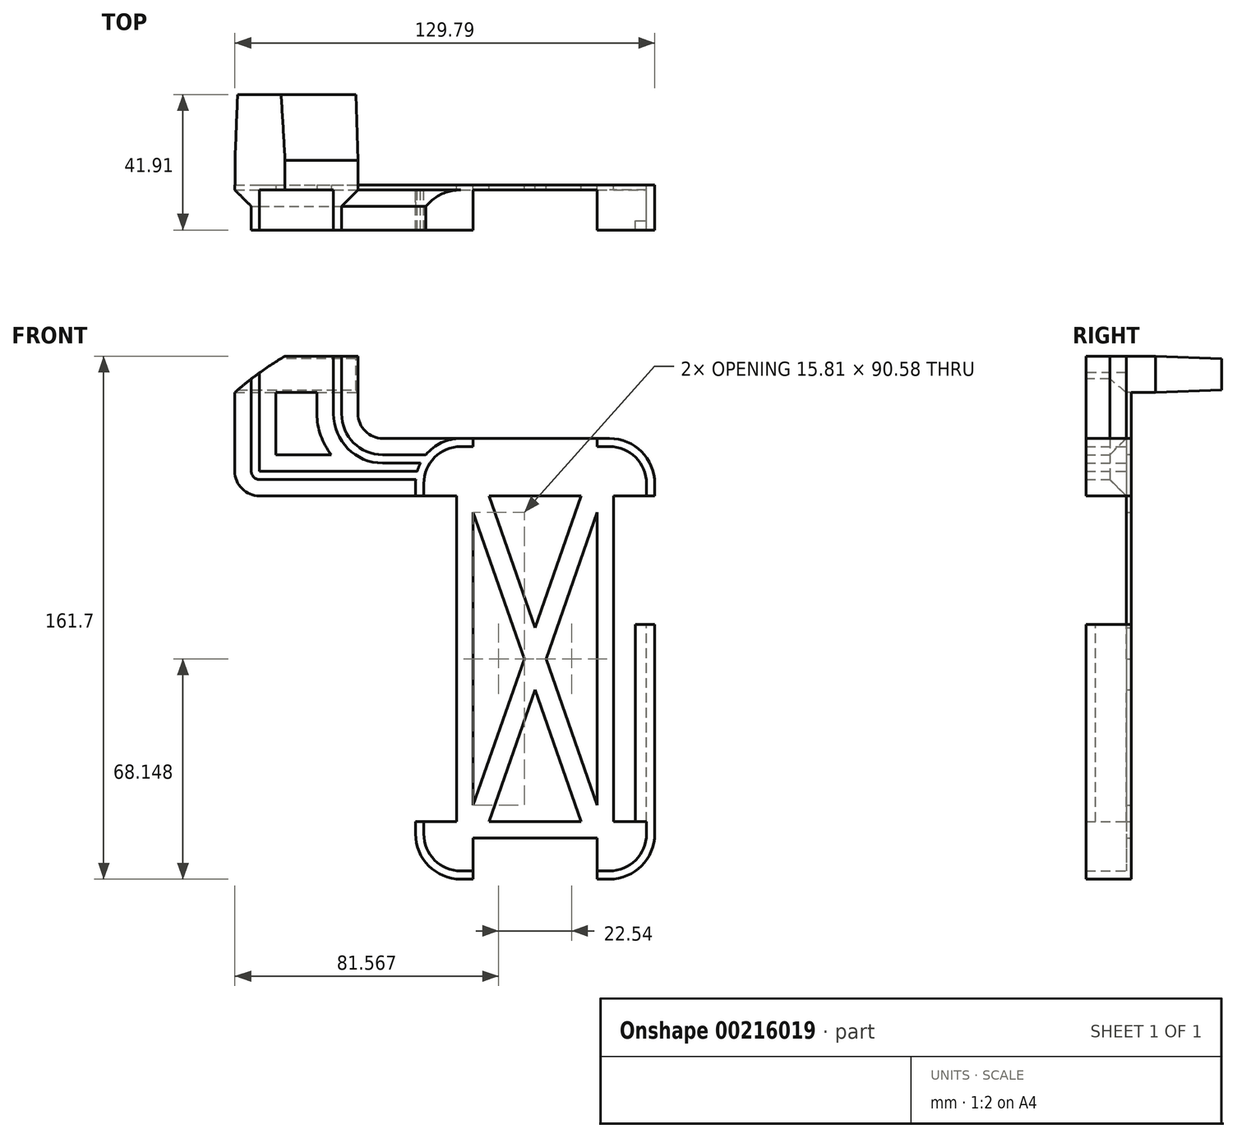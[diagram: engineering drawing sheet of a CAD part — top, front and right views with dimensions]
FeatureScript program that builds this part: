
annotation { "Feature Type Name" : "Feature", "Feature Type Description" : "" }
export const myFeature = defineFeature(function(context is Context, id is Id, definition is map)
    precondition{}
    {
        {
            var Q0;
            Q0=qCreatedBy(makeId("Front.planeOp"),FACE);
            var sketch = newSketch(context, id + "F0", { "sketchPlane" : qUnion([Q0])});
            skLineSegment(sketch, "E0.bottom", {"start": v(-38.1, 11.18) * mm, "end": v(0, 11.18) * mm});
            skLineSegment(sketch, "E0.top", {"start": v(-38.1, 0) * mm, "end": v(0, 0) * mm});
            skLineSegment(sketch, "E0.left", {"start": v(-38.1, 11.18) * mm, "end": v(-38.1, 0) * mm});
            skLineSegment(sketch, "E0.right", {"start": v(0, 11.18) * mm, "end": v(0, 0) * mm});
            skSolve(sketch);
        }
        {
            var Q0;
            Q0=makeQuery(id+"F0.imprint","IMPRINT",FACE,{"disambiguationData":[TD([[makeQuery(id+"F0.imprint","IMPRINT",EDGE,{"derivedFrom":sQuery(id+"F0.wireOp",EDGE,"E0.bottom")}),-1.0]])]});
            extrude(context, id + "F1", {"entities" : qUnion([Q0]), "oppositeDirection" : true, "depth" : 20.32 * mm, "hasDraft" : true, "draftAngle" : 2 * degree, "draftPullDirection" : true, "hasSecondDirection" : true, "secondDirectionOppositeDirection" : false, "secondDirectionDepth" : 7.62 * mm});
        }
        {
            var Q0;
            Q0=makeQuery(id+"F1.opExtrude","CAP_FACE",FACE,{"disambiguationData":[OSD([sQuery(id+"F0.wireOp",EDGE,"E0.bottom"),sQuery(id+"F0.wireOp",EDGE,"E0.top"),sQuery(id+"F0.wireOp",EDGE,"E0.left"),sQuery(id+"F0.wireOp",EDGE,"E0.right")])],"isStart":true});
            var sketch = newSketch(context, id + "F2", { "sketchPlane" : qUnion([Q0])});
            skLineSegment(sketch, "E1.0", {"start": v(31.75, -16.76) * mm, "end": v(77.72, -16.76) * mm});
            skLineSegment(sketch, "E1.1", {"start": v(20.32, -28.2) * mm, "end": v(20.32, -136.55) * mm});
            skLineSegment(sketch, "E1.2", {"start": v(31.75, -147.98) * mm, "end": v(77.72, -147.98) * mm});
            skLineSegment(sketch, "E1.3", {"start": v(89.15, -28.2) * mm, "end": v(89.15, -136.55) * mm});
            skPoint(sketch, "E2.visualSharp", {"position": v(20.32, -16.76) * mm});
            skArc(sketch, "E2.filletArc", {"start": v(31.75, -16.76) * mm, "mid": v(23.67, -20.11) * mm, "end": v(20.32, -28.2) * mm});
            skPoint(sketch, "E3.visualSharp", {"position": v(89.15, -16.76) * mm});
            skArc(sketch, "E3.filletArc", {"start": v(89.15, -28.2) * mm, "mid": v(85.8, -20.11) * mm, "end": v(77.72, -16.76) * mm});
            skPoint(sketch, "E4.visualSharp", {"position": v(89.15, -147.98) * mm});
            skArc(sketch, "E4.filletArc", {"start": v(77.72, -147.98) * mm, "mid": v(85.8, -144.63) * mm, "end": v(89.15, -136.55) * mm});
            skPoint(sketch, "E5.visualSharp", {"position": v(20.32, -147.98) * mm});
            skArc(sketch, "E5.filletArc", {"start": v(20.32, -136.55) * mm, "mid": v(23.67, -144.63) * mm, "end": v(31.75, -147.98) * mm});
            skArc(sketch, "E6.0", {"start": v(31.75, -14.22) * mm, "mid": v(21.87, -18.32) * mm, "end": v(17.78, -28.2) * mm});
            skLineSegment(sketch, "E6.1", {"start": v(17.78, -28.2) * mm, "end": v(17.78, -136.55) * mm});
            skLineSegment(sketch, "E6.2", {"start": v(31.75, -14.22) * mm, "end": v(77.72, -14.22) * mm});
            skArc(sketch, "E6.3", {"start": v(17.78, -136.55) * mm, "mid": v(21.87, -146.43) * mm, "end": v(31.75, -150.52) * mm});
            skArc(sketch, "E6.4", {"start": v(91.7, -28.2) * mm, "mid": v(87.6, -18.32) * mm, "end": v(77.72, -14.22) * mm});
            skLineSegment(sketch, "E6.5", {"start": v(91.7, -28.2) * mm, "end": v(91.7, -136.55) * mm});
            skArc(sketch, "E6.6", {"start": v(77.72, -150.52) * mm, "mid": v(87.6, -146.43) * mm, "end": v(91.7, -136.55) * mm});
            skLineSegment(sketch, "E6.7", {"start": v(31.75, -150.52) * mm, "end": v(77.72, -150.52) * mm});
            skLineSegment(sketch, "E7", {"start": v(17.78, -32) * mm, "end": v(91.7, -32) * mm});
            skLineSegment(sketch, "E8", {"start": v(35.56, -14.22) * mm, "end": v(35.56, -150.52) * mm});
            skLineSegment(sketch, "E9", {"start": v(73.91, -14.22) * mm, "end": v(73.91, -150.52) * mm});
            skLineSegment(sketch, "E10", {"start": v(17.78, -132.74) * mm, "end": v(91.7, -132.74) * mm});
            skLineSegment(sketch, "E11", {"start": v(30.48, -32) * mm, "end": v(30.48, -132.74) * mm});
            skLineSegment(sketch, "E12", {"start": v(79, -32) * mm, "end": v(79, -132.74) * mm});
            skLineSegment(sketch, "E13", {"start": v(35.56, -26.92) * mm, "end": v(73.91, -26.92) * mm});
            skLineSegment(sketch, "E14", {"start": v(35.56, -137.82) * mm, "end": v(73.91, -137.82) * mm});
            skLineSegment(sketch, "E15", {"start": v(35.56, -37.08) * mm, "end": v(68.96, -132.74) * mm});
            skLineSegment(sketch, "E16", {"start": v(40.51, -32) * mm, "end": v(73.91, -127.66) * mm});
            skLineSegment(sketch, "E17", {"start": v(35.56, -127.66) * mm, "end": v(68.96, -32) * mm});
            skLineSegment(sketch, "E18", {"start": v(40.51, -132.74) * mm, "end": v(73.91, -37.08) * mm});
            skSolve(sketch);
        }
        {
            var Q0;
            {var subQ0=sQuery(id+"F2.wireOp",EDGE,"E2.filletArc");Q0=makeQuery(id+"F2.imprint","IMPRINT",FACE,{"disambiguationData":[TD([[makeQuery(id+"F2.imprint","IMPRINT",EDGE,{"derivedFrom":subQ0}),-1.0]])]});}
            var Q1;
            {var subQ0=sQuery(id+"F2.wireOp",EDGE,"E3.filletArc");Q1=makeQuery(id+"F2.imprint","IMPRINT",FACE,{"disambiguationData":[TD([[makeQuery(id+"F2.imprint","IMPRINT",EDGE,{"derivedFrom":subQ0}),-1.0]])]});}
            var Q2;
            {var subQ4=sQuery(id+"F2.wireOp",EDGE,"E5.filletArc");Q2=makeQuery(id+"F2.imprint","IMPRINT",FACE,{"disambiguationData":[TD([[makeQuery(id+"F2.imprint","IMPRINT",EDGE,{"derivedFrom":subQ4}),-1.0]])]});}
            var Q3;
            {var subQ4=sQuery(id+"F2.wireOp",EDGE,"E4.filletArc");Q3=makeQuery(id+"F2.imprint","IMPRINT",FACE,{"disambiguationData":[TD([[makeQuery(id+"F2.imprint","IMPRINT",EDGE,{"derivedFrom":subQ4}),-1.0]])]});}
            extrude(context, id + "F3", {"entities" : qUnion([Q0, Q1, Q2, Q3]), "depth" : 13.97 * mm});
        }
        {
            var Q0;
            {var subQ4=sQuery(id+"F2.wireOp",EDGE,"E2.filletArc");Q0=makeQuery(id+"F2.imprint","IMPRINT",FACE,{"disambiguationData":[TD([[makeQuery(id+"F2.imprint","IMPRINT",EDGE,{"derivedFrom":subQ4}),1.0]])]});}
            var Q1;
            {var subQ0=sQuery(id+"F2.wireOp",EDGE,"E3.filletArc");Q1=makeQuery(id+"F2.imprint","IMPRINT",FACE,{"disambiguationData":[TD([[makeQuery(id+"F2.imprint","IMPRINT",EDGE,{"derivedFrom":subQ0}),1.0]])]});}
            var Q2;
            {var subQ0=sQuery(id+"F2.wireOp",EDGE,"E5.filletArc");Q2=makeQuery(id+"F2.imprint","IMPRINT",FACE,{"disambiguationData":[TD([[makeQuery(id+"F2.imprint","IMPRINT",EDGE,{"derivedFrom":subQ0}),1.0]])]});}
            var Q3;
            {var subQ0=sQuery(id+"F2.wireOp",EDGE,"E4.filletArc");Q3=makeQuery(id+"F2.imprint","IMPRINT",FACE,{"disambiguationData":[TD([[makeQuery(id+"F2.imprint","IMPRINT",EDGE,{"derivedFrom":subQ0}),1.0]])]});}
            var Q4;
            {var subQ3=sQuery(id+"F2.wireOp",EDGE,"E11");Q4=makeQuery(id+"F2.imprint","IMPRINT",FACE,{"disambiguationData":[TD([[makeQuery(id+"F2.imprint","IMPRINT",EDGE,{"derivedFrom":subQ3}),1.0]])]});}
            var Q5;
            {var subQ5=sQuery(id+"F2.wireOp",EDGE,"E7");var subQ7=sQuery(id+"F2.wireOp",EDGE,"E16");var subQ8=makeQuery(id+"F2.imprint","INTERSECT",VERTEX,{"derivedFrom":[subQ5,subQ7]});Q5=makeQuery(id+"F2.imprint","IMPRINT",FACE,{"disambiguationData":[TD([[makeQuery(id+"F2.imprint","IMPRINT",EDGE,{"disambiguationData":[TD([[subQ8,1.0]])],"derivedFrom":subQ5}),-1.0]])]});}
            var Q6;
            {var subQ3=sQuery(id+"F2.wireOp",EDGE,"E13");Q6=makeQuery(id+"F2.imprint","IMPRINT",FACE,{"disambiguationData":[TD([[makeQuery(id+"F2.imprint","IMPRINT",EDGE,{"derivedFrom":subQ3}),-1.0]])]});}
            var Q7;
            {var subQ4=sQuery(id+"F2.wireOp",EDGE,"E12");Q7=makeQuery(id+"F2.imprint","IMPRINT",FACE,{"disambiguationData":[TD([[makeQuery(id+"F2.imprint","IMPRINT",EDGE,{"derivedFrom":subQ4}),-1.0]])]});}
            var Q8;
            {var subQ0=sQuery(id+"F2.wireOp",EDGE,"E17");var subQ1=sQuery(id+"F2.wireOp",EDGE,"E15");var subQ2=makeQuery(id+"F2.imprint","INTERSECT",VERTEX,{"derivedFrom":[subQ1,subQ0]});Q8=makeQuery(id+"F2.imprint","IMPRINT",FACE,{"disambiguationData":[TD([[makeQuery(id+"F2.imprint","IMPRINT",EDGE,{"disambiguationData":[TD([[subQ2,-1.0]])],"derivedFrom":subQ1}),1.0]])]});}
            var Q9;
            {var subQ0=sQuery(id+"F2.wireOp",EDGE,"E17");var subQ1=sQuery(id+"F2.wireOp",EDGE,"E7");var subQ2=makeQuery(id+"F2.imprint","INTERSECT",VERTEX,{"derivedFrom":[subQ1,subQ0]});Q9=makeQuery(id+"F2.imprint","IMPRINT",FACE,{"disambiguationData":[TD([[makeQuery(id+"F2.imprint","IMPRINT",EDGE,{"disambiguationData":[TD([[subQ2,-1.0]])],"derivedFrom":subQ1}),-1.0]])]});}
            var Q10;
            {var subQ0=sQuery(id+"F2.wireOp",EDGE,"E16");var subQ1=sQuery(id+"F2.wireOp",EDGE,"E9");var subQ2=makeQuery(id+"F2.imprint","INTERSECT",VERTEX,{"derivedFrom":[subQ1,subQ0]});Q10=makeQuery(id+"F2.imprint","IMPRINT",FACE,{"disambiguationData":[TD([[makeQuery(id+"F2.imprint","IMPRINT",EDGE,{"disambiguationData":[TD([[subQ2,-1.0]])],"derivedFrom":subQ1}),-1.0]])]});}
            var Q11;
            {var subQ0=sQuery(id+"F2.wireOp",EDGE,"E17");var subQ7=sQuery(id+"F2.wireOp",EDGE,"E8");var subQ9=makeQuery(id+"F2.imprint","INTERSECT",VERTEX,{"derivedFrom":[subQ7,subQ0]});Q11=makeQuery(id+"F2.imprint","IMPRINT",FACE,{"disambiguationData":[TD([[makeQuery(id+"F2.imprint","IMPRINT",EDGE,{"disambiguationData":[TD([[subQ9,-1.0]])],"derivedFrom":subQ7}),1.0]])]});}
            var Q12;
            {var subQ4=sQuery(id+"F2.wireOp",EDGE,"E14");Q12=makeQuery(id+"F2.imprint","IMPRINT",FACE,{"disambiguationData":[TD([[makeQuery(id+"F2.imprint","IMPRINT",EDGE,{"derivedFrom":subQ4}),1.0]])]});}
            extrude(context, id + "F4", {"entities" : qUnion([Q0, Q1, Q2, Q3, Q4, Q5, Q6, Q7, Q8, Q9, Q10, Q11, Q12]), "depth" : 1.52 * mm});
        }
        {
            var Q0;
            Q0=makeQuery(id+"F1.opExtrude","CAP_FACE",FACE,{"disambiguationData":[OSD([sQuery(id+"F0.wireOp",EDGE,"E0.bottom"),sQuery(id+"F0.wireOp",EDGE,"E0.top"),sQuery(id+"F0.wireOp",EDGE,"E0.left"),sQuery(id+"F0.wireOp",EDGE,"E0.right")])],"isStart":true});
            var sketch = newSketch(context, id + "F5", { "sketchPlane" : qUnion([Q0])});
            skLineSegment(sketch, "E19.bottom", {"start": v(-38.1, 11.18) * mm, "end": v(0, 11.18) * mm});
            skLineSegment(sketch, "E19.top", {"start": v(-30.48, -32) * mm, "end": v(91.7, -32) * mm});
            skLineSegment(sketch, "E19.left", {"start": v(-38.1, 11.18) * mm, "end": v(-38.1, -24.38) * mm});
            skLineSegment(sketch, "E19.right", {"start": v(91.7, -28.2) * mm, "end": v(91.7, -32) * mm});
            skLineSegment(sketch, "E20", {"start": v(77.72, -14.22) * mm, "end": v(7.62, -14.22) * mm});
            skArc(sketch, "E21.0", {"start": v(91.7, -28.2) * mm, "mid": v(87.6, -18.32) * mm, "end": v(77.72, -14.22) * mm});
            skLineSegment(sketch, "E22", {"start": v(0, 0) * mm, "end": v(0, -6.6) * mm});
            skLineSegment(sketch, "E23", {"start": v(0, 0) * mm, "end": v(0, 11.18) * mm});
            skPoint(sketch, "E24.visualSharp", {"position": v(0, -14.22) * mm});
            skArc(sketch, "E24.filletArc", {"start": v(0, -6.6) * mm, "mid": v(2.23, -12) * mm, "end": v(7.62, -14.22) * mm});
            skPoint(sketch, "E25.visualSharp", {"position": v(-38.1, -32) * mm});
            skArc(sketch, "E25.filletArc", {"start": v(-38.1, -24.38) * mm, "mid": v(-35.87, -29.77) * mm, "end": v(-30.48, -32) * mm});
            skSolve(sketch);
        }
        {
            var Q0;
            Q0 = qSketchRegion(id + "F5", true);
            extrude(context, id + "F6", {"entities" : qUnion([Q0]), "depth" : 1.52 * mm});
        }
        {
            var Q0;
            Q0=makeQuery(id+"F3.opExtrude","SWEPT_BODY",BODY,{"disambiguationData":[OSD([sQuery(id+"F2.wireOp",EDGE,"E1.0"),sQuery(id+"F2.wireOp",EDGE,"E1.1"),sQuery(id+"F2.wireOp",EDGE,"E2.filletArc"),sQuery(id+"F2.wireOp",EDGE,"E6.0"),sQuery(id+"F2.wireOp",EDGE,"E6.1"),sQuery(id+"F2.wireOp",EDGE,"E6.2"),sQuery(id+"F2.wireOp",EDGE,"E7"),sQuery(id+"F2.wireOp",EDGE,"E8")])]});
            var Q1;
            Q1=makeQuery(id+"F3.opExtrude","SWEPT_BODY",BODY,{"disambiguationData":[OSD([sQuery(id+"F2.wireOp",EDGE,"E1.0"),sQuery(id+"F2.wireOp",EDGE,"E1.3"),sQuery(id+"F2.wireOp",EDGE,"E3.filletArc"),sQuery(id+"F2.wireOp",EDGE,"E6.2"),sQuery(id+"F2.wireOp",EDGE,"E6.4"),sQuery(id+"F2.wireOp",EDGE,"E6.5"),sQuery(id+"F2.wireOp",EDGE,"E7"),sQuery(id+"F2.wireOp",EDGE,"E9")])]});
            var Q2;
            Q2=makeQuery(id+"F3.opExtrude","SWEPT_BODY",BODY,{"disambiguationData":[OSD([sQuery(id+"F2.wireOp",EDGE,"E1.1"),sQuery(id+"F2.wireOp",EDGE,"E1.2"),sQuery(id+"F2.wireOp",EDGE,"E5.filletArc"),sQuery(id+"F2.wireOp",EDGE,"E6.1"),sQuery(id+"F2.wireOp",EDGE,"E6.3"),sQuery(id+"F2.wireOp",EDGE,"E6.7"),sQuery(id+"F2.wireOp",EDGE,"E8"),sQuery(id+"F2.wireOp",EDGE,"E10")])]});
            var Q3;
            Q3=makeQuery(id+"F3.opExtrude","SWEPT_BODY",BODY,{"disambiguationData":[OSD([sQuery(id+"F2.wireOp",EDGE,"E1.2"),sQuery(id+"F2.wireOp",EDGE,"E1.3"),sQuery(id+"F2.wireOp",EDGE,"E4.filletArc"),sQuery(id+"F2.wireOp",EDGE,"E6.5"),sQuery(id+"F2.wireOp",EDGE,"E6.6"),sQuery(id+"F2.wireOp",EDGE,"E6.7"),sQuery(id+"F2.wireOp",EDGE,"E9"),sQuery(id+"F2.wireOp",EDGE,"E10")])]});
            var Q4;
            Q4=makeQuery(id+"F4.opExtrude","SWEPT_BODY",BODY,{"disambiguationData":[OSD([sQuery(id+"F2.wireOp",EDGE,"E1.0"),sQuery(id+"F2.wireOp",EDGE,"E1.1"),sQuery(id+"F2.wireOp",EDGE,"E1.2"),sQuery(id+"F2.wireOp",EDGE,"E1.3"),sQuery(id+"F2.wireOp",EDGE,"E2.filletArc"),sQuery(id+"F2.wireOp",EDGE,"E3.filletArc"),sQuery(id+"F2.wireOp",EDGE,"E4.filletArc"),sQuery(id+"F2.wireOp",EDGE,"E5.filletArc"),sQuery(id+"F2.wireOp",EDGE,"E7"),sQuery(id+"F2.wireOp",EDGE,"E8"),sQuery(id+"F2.wireOp",EDGE,"E9"),sQuery(id+"F2.wireOp",EDGE,"E10"),sQuery(id+"F2.wireOp",EDGE,"E11"),sQuery(id+"F2.wireOp",EDGE,"E12"),sQuery(id+"F2.wireOp",EDGE,"E13"),sQuery(id+"F2.wireOp",EDGE,"E14"),sQuery(id+"F2.wireOp",EDGE,"E15"),sQuery(id+"F2.wireOp",EDGE,"E16"),sQuery(id+"F2.wireOp",EDGE,"E17"),sQuery(id+"F2.wireOp",EDGE,"E18")])]});
            var Q5;
            Q5=makeQuery(id+"F6.opExtrude","SWEPT_BODY",BODY,{"disambiguationData":[OSD([sQuery(id+"F5.wireOp",EDGE,"E19.bottom"),sQuery(id+"F5.wireOp",EDGE,"E19.top"),sQuery(id+"F5.wireOp",EDGE,"E19.left"),sQuery(id+"F5.wireOp",EDGE,"E19.right"),sQuery(id+"F5.wireOp",EDGE,"E20"),sQuery(id+"F5.wireOp",EDGE,"E21.0"),sQuery(id+"F5.wireOp",EDGE,"E22"),sQuery(id+"F5.wireOp",EDGE,"E23"),sQuery(id+"F5.wireOp",EDGE,"E24.filletArc"),sQuery(id+"F5.wireOp",EDGE,"E25.filletArc")])]});
            var Q6;
            Q6=makeQuery(id+"F1.split0.splitOp","SPLIT",BODY,{"derivedFrom":makeQuery(id+"F1.opExtrude","SWEPT_BODY",BODY,{"disambiguationData":[OSD([sQuery(id+"F0.wireOp",EDGE,"E0.bottom"),sQuery(id+"F0.wireOp",EDGE,"E0.top"),sQuery(id+"F0.wireOp",EDGE,"E0.left"),sQuery(id+"F0.wireOp",EDGE,"E0.right")])]})});
            booleanBodies(context, id + "F7", {"operationType" : BooleanOperationType.UNION, "tools" : qUnion([Q0, Q1, Q2, Q3, Q4, Q5, Q6])});
        }
        {
            var Q0;
            Q0=makeQuery(id+"F7.opBoolean","MERGE",FACE,{"disambiguationData":[OD(0.0)],"derivedFrom":[makeQuery(id+"F4.opExtrude","CAP_FACE",FACE,{"disambiguationData":[OSD([sQuery(id+"F2.wireOp",EDGE,"E1.0"),sQuery(id+"F2.wireOp",EDGE,"E1.1"),sQuery(id+"F2.wireOp",EDGE,"E1.2"),sQuery(id+"F2.wireOp",EDGE,"E1.3"),sQuery(id+"F2.wireOp",EDGE,"E2.filletArc"),sQuery(id+"F2.wireOp",EDGE,"E3.filletArc"),sQuery(id+"F2.wireOp",EDGE,"E4.filletArc"),sQuery(id+"F2.wireOp",EDGE,"E5.filletArc"),sQuery(id+"F2.wireOp",EDGE,"E7"),sQuery(id+"F2.wireOp",EDGE,"E8"),sQuery(id+"F2.wireOp",EDGE,"E9"),sQuery(id+"F2.wireOp",EDGE,"E10"),sQuery(id+"F2.wireOp",EDGE,"E11"),sQuery(id+"F2.wireOp",EDGE,"E12"),sQuery(id+"F2.wireOp",EDGE,"E13"),sQuery(id+"F2.wireOp",EDGE,"E14"),sQuery(id+"F2.wireOp",EDGE,"E15"),sQuery(id+"F2.wireOp",EDGE,"E16"),sQuery(id+"F2.wireOp",EDGE,"E17"),sQuery(id+"F2.wireOp",EDGE,"E18")])],"isStart":false}),makeQuery(id+"F6.opExtrude","CAP_FACE",FACE,{"disambiguationData":[OSD([sQuery(id+"F5.wireOp",EDGE,"E19.bottom"),sQuery(id+"F5.wireOp",EDGE,"E19.top"),sQuery(id+"F5.wireOp",EDGE,"E19.left"),sQuery(id+"F5.wireOp",EDGE,"E19.right"),sQuery(id+"F5.wireOp",EDGE,"E20"),sQuery(id+"F5.wireOp",EDGE,"E21.0"),sQuery(id+"F5.wireOp",EDGE,"E22"),sQuery(id+"F5.wireOp",EDGE,"E23"),sQuery(id+"F5.wireOp",EDGE,"E24.filletArc"),sQuery(id+"F5.wireOp",EDGE,"E25.filletArc")])],"isStart":false})]});
            var sketch = newSketch(context, id + "F8", { "sketchPlane" : qUnion([Q0])});
            skLineSegment(sketch, "E26.0", {"start": v(-30.48, -26.92) * mm, "end": v(17.84, -26.92) * mm});
            skArc(sketch, "E26.1", {"start": v(-33.02, -24.38) * mm, "mid": v(-32.28, -26.18) * mm, "end": v(-30.48, -26.92) * mm});
            skLineSegment(sketch, "E26.2", {"start": v(-33.02, 11.18) * mm, "end": v(-33.02, -24.38) * mm});
            skLineSegment(sketch, "E27.0", {"start": v(-30.48, -24.38) * mm, "end": v(18.3, -24.38) * mm});
            skLineSegment(sketch, "E27.1", {"start": v(-30.48, 11.18) * mm, "end": v(-30.48, -24.38) * mm});
            skLineSegment(sketch, "E28", {"start": v(-33.02, 11.18) * mm, "end": v(-30.48, 11.18) * mm});
            skArc(sketch, "E29.0", {"start": v(18.3, -24.38) * mm, "mid": v(18.01, -25.64) * mm, "end": v(17.84, -26.92) * mm});
            skPoint(sketch, "E30.orphan", {"position": v(31.75, -14.22) * mm});
            skPoint(sketch, "E31.orphan", {"position": v(17.78, -28.2) * mm});
            skLineSegment(sketch, "E32.0", {"start": v(20.97, -19.3) * mm, "end": v(7.62, -19.3) * mm});
            skArc(sketch, "E32.1", {"start": v(-5.08, -6.6) * mm, "mid": v(-1.36, -15.58) * mm, "end": v(7.62, -19.3) * mm});
            skLineSegment(sketch, "E32.2", {"start": v(-5.08, 11.18) * mm, "end": v(-5.08, -6.6) * mm});
            skLineSegment(sketch, "E33.0", {"start": v(19.3, -21.84) * mm, "end": v(7.62, -21.84) * mm});
            skArc(sketch, "E33.1", {"start": v(-7.62, -6.6) * mm, "mid": v(-3.16, -17.38) * mm, "end": v(7.62, -21.84) * mm});
            skLineSegment(sketch, "E33.2", {"start": v(-7.62, 11.18) * mm, "end": v(-7.62, -6.6) * mm});
            skLineSegment(sketch, "E34", {"start": v(-5.08, 11.18) * mm, "end": v(-7.62, 11.18) * mm});
            skArc(sketch, "E35", {"start": v(20.97, -19.3) * mm, "mid": v(20.07, -20.53) * mm, "end": v(19.3, -21.84) * mm});
            skSolve(sketch);
        }
        {
            var Q0;
            Q0 = qSketchRegion(id + "F8", true);
            extrude(context, id + "F9", {"entities" : qUnion([Q0]), "operationType" : NewBodyOperationType.ADD, "depth" : 12.45 * mm});
        }
        {
            var Q0;
            {var subQ0=sQuery(id+"F2.wireOp",EDGE,"E10");var subQ1=sQuery(id+"F2.wireOp",EDGE,"E9");var subQ2=sQuery(id+"F2.wireOp",EDGE,"E8");var subQ3=sQuery(id+"F2.wireOp",EDGE,"E7");var subQ4=sQuery(id+"F2.wireOp",EDGE,"E5.filletArc");var subQ5=sQuery(id+"F2.wireOp",EDGE,"E4.filletArc");var subQ6=sQuery(id+"F2.wireOp",EDGE,"E3.filletArc");var subQ7=sQuery(id+"F2.wireOp",EDGE,"E2.filletArc");var subQ8=sQuery(id+"F2.wireOp",EDGE,"E1.3");var subQ9=sQuery(id+"F2.wireOp",EDGE,"E1.2");var subQ10=sQuery(id+"F2.wireOp",EDGE,"E1.1");var subQ11=sQuery(id+"F2.wireOp",EDGE,"E1.0");var subQ12=sQuery(id+"F2.wireOp",EDGE,"E6.7");var subQ13=sQuery(id+"F2.wireOp",EDGE,"E6.5");var subQ14=sQuery(id+"F2.wireOp",EDGE,"E6.1");var subQ15=sQuery(id+"F2.wireOp",EDGE,"E6.2");Q0=makeQuery(id+"F7.opBoolean","MERGE",FACE,{"derivedFrom":[makeQuery(id+"F3.opExtrude","CAP_FACE",FACE,{"disambiguationData":[OSD([subQ11,subQ10,subQ7,sQuery(id+"F2.wireOp",EDGE,"E6.0"),subQ14,subQ15,subQ3,subQ2])],"isStart":true}),makeQuery(id+"F3.opExtrude","CAP_FACE",FACE,{"disambiguationData":[OSD([subQ11,subQ8,subQ6,subQ15,sQuery(id+"F2.wireOp",EDGE,"E6.4"),subQ13,subQ3,subQ1])],"isStart":true}),makeQuery(id+"F3.opExtrude","CAP_FACE",FACE,{"disambiguationData":[OSD([subQ10,subQ9,subQ4,subQ14,sQuery(id+"F2.wireOp",EDGE,"E6.3"),subQ12,subQ2,subQ0])],"isStart":true}),makeQuery(id+"F3.opExtrude","CAP_FACE",FACE,{"disambiguationData":[OSD([subQ9,subQ8,subQ5,subQ13,sQuery(id+"F2.wireOp",EDGE,"E6.6"),subQ12,subQ1,subQ0])],"isStart":true}),makeQuery(id+"F4.opExtrude","CAP_FACE",FACE,{"disambiguationData":[OSD([subQ11,subQ10,subQ9,subQ8,subQ7,subQ6,subQ5,subQ4,subQ3,subQ2,subQ1,subQ0,sQuery(id+"F2.wireOp",EDGE,"E11"),sQuery(id+"F2.wireOp",EDGE,"E12"),sQuery(id+"F2.wireOp",EDGE,"E13"),sQuery(id+"F2.wireOp",EDGE,"E14"),sQuery(id+"F2.wireOp",EDGE,"E15"),sQuery(id+"F2.wireOp",EDGE,"E16"),sQuery(id+"F2.wireOp",EDGE,"E17"),sQuery(id+"F2.wireOp",EDGE,"E18")])],"isStart":true}),makeQuery(id+"F6.opExtrude","CAP_FACE",FACE,{"disambiguationData":[OSD([sQuery(id+"F5.wireOp",EDGE,"E19.bottom"),sQuery(id+"F5.wireOp",EDGE,"E19.top"),sQuery(id+"F5.wireOp",EDGE,"E19.left"),sQuery(id+"F5.wireOp",EDGE,"E19.right"),sQuery(id+"F5.wireOp",EDGE,"E20"),sQuery(id+"F5.wireOp",EDGE,"E21.0"),sQuery(id+"F5.wireOp",EDGE,"E22"),sQuery(id+"F5.wireOp",EDGE,"E23"),sQuery(id+"F5.wireOp",EDGE,"E24.filletArc"),sQuery(id+"F5.wireOp",EDGE,"E25.filletArc")])],"isStart":true})]});}
            var sketch = newSketch(context, id + "F10", { "sketchPlane" : qUnion([Q0])});
            skLineSegment(sketch, "E36.bottom", {"start": v(-85.73, -71.78) * mm, "end": v(-91.7, -71.78) * mm});
            skLineSegment(sketch, "E36.top", {"start": v(-85.73, -132.74) * mm, "end": v(-91.7, -132.74) * mm});
            skLineSegment(sketch, "E36.left", {"start": v(-85.73, -71.78) * mm, "end": v(-85.73, -132.74) * mm});
            skLineSegment(sketch, "E36.right", {"start": v(-91.7, -71.78) * mm, "end": v(-91.7, -132.74) * mm});
            skLineSegment(sketch, "E37", {"start": v(-89.15, -132.74) * mm, "end": v(-89.15, -71.78) * mm});
            skSolve(sketch);
        }
        {
            var Q0;
            {var subQ0=sQuery(id+"F10.wireOp",EDGE,"E36.right");Q0=makeQuery(id+"F10.imprint","IMPRINT",FACE,{"disambiguationData":[TD([[makeQuery(id+"F10.imprint","IMPRINT",EDGE,{"derivedFrom":subQ0}),1.0]])]});}
            var Q1;
            {var subQ0=sQuery(id+"F10.wireOp",EDGE,"E36.left");Q1=makeQuery(id+"F10.imprint","IMPRINT",FACE,{"disambiguationData":[TD([[makeQuery(id+"F10.imprint","IMPRINT",EDGE,{"derivedFrom":subQ0}),-1.0]])]});}
            extrude(context, id + "F11", {"entities" : qUnion([Q0, Q1]), "operationType" : NewBodyOperationType.ADD, "oppositeDirection" : true, "depth" : 13.97 * mm});
        }
        {
            var Q0;
            {var subQ0=sQuery(id+"F10.wireOp",EDGE,"E36.left");Q0=makeQuery(id+"F10.imprint","IMPRINT",FACE,{"disambiguationData":[TD([[makeQuery(id+"F10.imprint","IMPRINT",EDGE,{"derivedFrom":subQ0}),-1.0]])]});}
            extrude(context, id + "F12", {"entities" : qUnion([Q0]), "operationType" : NewBodyOperationType.REMOVE, "oppositeDirection" : true, "depth" : 11.05 * mm});
        }
        {
            var Q0;
            Q0=qCreatedBy(makeId("Front.planeOp"),FACE);
            var sketch = newSketch(context, id + "F13", { "sketchPlane" : qUnion([Q0])});
            skCircle(sketch, "E38", {"center": v(25.92, -72.28) * mm, "radius": 96.52 * mm});
            skCircle(sketch, "E39", {"center": v(25.92, -72.28) * mm, "radius": 117.82 * mm});
            skSolve(sketch);
        }
        {
            var Q0;
            Q0 = qSketchRegion(id + "F13", true);
            extrude(context, id + "F14", {"entities" : qUnion([Q0]), "operationType" : NewBodyOperationType.REMOVE, "endBound" : BoundingType.THROUGH_ALL, "oppositeDirection" : true, "depth" : 25.4 * mm, "hasSecondDirection" : true, "secondDirectionBound" : SecondDirectionBoundingType.THROUGH_ALL, "secondDirectionOppositeDirection" : false, "secondDirectionDepth" : 25.4 * mm});
        }
        {
            var Q0;
            Q0=makeQuery(id+"F9.opExtrude","CAP_EDGE",EDGE,{"disambiguationData":[OSD([sQuery(id+"F8.wireOp",EDGE,"E26.0")])],"isStart":true});
            var Q1;
            Q1=makeQuery(id+"F9.opExtrude","CAP_EDGE",EDGE,{"disambiguationData":[OSD([sQuery(id+"F8.wireOp",EDGE,"E27.1")])],"isStart":true});
            var Q2;
            Q2=makeQuery(id+"F9.opExtrude","CAP_EDGE",EDGE,{"disambiguationData":[OSD([sQuery(id+"F8.wireOp",EDGE,"E27.0")])],"isStart":true});
            var Q3;
            Q3=makeQuery(id+"F9.opExtrude","CAP_EDGE",EDGE,{"disambiguationData":[OSD([sQuery(id+"F8.wireOp",EDGE,"E33.1")])],"isStart":true});
            var Q4;
            Q4=makeQuery(id+"F9.opExtrude","CAP_EDGE",EDGE,{"disambiguationData":[OSD([sQuery(id+"F8.wireOp",EDGE,"E32.2")])],"isStart":true});
            chamfer(context, id + "F15", {"entities" : qUnion([Q0, Q1, Q2, Q3, Q4]), "width" : 5.08 * mm, "tangentPropagation" : true});
        }
        {
            var Q0;
            {var subQ0=sQuery(id+"F5.wireOp",EDGE,"E19.bottom");Q0=makeQuery(id+"F9.boolean.opBoolean","SPLIT",FACE,{"disambiguationData":[TD([makeQuery(id+"F9.opExtrude","SWEPT_FACE",FACE,{"disambiguationData":[OSD([sQuery(id+"F8.wireOp",EDGE,"E27.0")])]})])],"derivedFrom":makeQuery(id+"F7.opBoolean","MERGE",FACE,{"disambiguationData":[OD(0.0)],"derivedFrom":[makeQuery(id+"F4.opExtrude","CAP_FACE",FACE,{"disambiguationData":[OSD([sQuery(id+"F2.wireOp",EDGE,"E1.0"),sQuery(id+"F2.wireOp",EDGE,"E1.1"),sQuery(id+"F2.wireOp",EDGE,"E1.2"),sQuery(id+"F2.wireOp",EDGE,"E1.3"),sQuery(id+"F2.wireOp",EDGE,"E2.filletArc"),sQuery(id+"F2.wireOp",EDGE,"E3.filletArc"),sQuery(id+"F2.wireOp",EDGE,"E4.filletArc"),sQuery(id+"F2.wireOp",EDGE,"E5.filletArc"),sQuery(id+"F2.wireOp",EDGE,"E7"),sQuery(id+"F2.wireOp",EDGE,"E8"),sQuery(id+"F2.wireOp",EDGE,"E9"),sQuery(id+"F2.wireOp",EDGE,"E10"),sQuery(id+"F2.wireOp",EDGE,"E11"),sQuery(id+"F2.wireOp",EDGE,"E12"),sQuery(id+"F2.wireOp",EDGE,"E13"),sQuery(id+"F2.wireOp",EDGE,"E14"),sQuery(id+"F2.wireOp",EDGE,"E15"),sQuery(id+"F2.wireOp",EDGE,"E16"),sQuery(id+"F2.wireOp",EDGE,"E17"),sQuery(id+"F2.wireOp",EDGE,"E18")])],"isStart":false}),makeQuery(id+"F6.opExtrude","CAP_FACE",FACE,{"disambiguationData":[OSD([subQ0,sQuery(id+"F5.wireOp",EDGE,"E19.top"),sQuery(id+"F5.wireOp",EDGE,"E19.left"),sQuery(id+"F5.wireOp",EDGE,"E19.right"),sQuery(id+"F5.wireOp",EDGE,"E20"),sQuery(id+"F5.wireOp",EDGE,"E21.0"),sQuery(id+"F5.wireOp",EDGE,"E22"),sQuery(id+"F5.wireOp",EDGE,"E23"),sQuery(id+"F5.wireOp",EDGE,"E24.filletArc"),sQuery(id+"F5.wireOp",EDGE,"E25.filletArc")])],"isStart":false})]})});}
            var sketch = newSketch(context, id + "F16", { "sketchPlane" : qUnion([Q0])});
            skLineSegment(sketch, "E40.0", {"start": v(-25.4, 0) * mm, "end": v(-25.4, -19.3) * mm});
            skLineSegment(sketch, "E40.1", {"start": v(-25.4, -19.3) * mm, "end": v(-8.24, -19.3) * mm});
            skArc(sketch, "E40.2", {"start": v(-8.24, -19.3) * mm, "mid": v(-11.55, -13.33) * mm, "end": v(-12.7, -6.6) * mm});
            skLineSegment(sketch, "E40.3", {"start": v(-12.7, -6.6) * mm, "end": v(-12.7, 0) * mm});
            skLineSegment(sketch, "E41.0", {"start": v(-25.4, 0) * mm, "end": v(-12.7, 0) * mm});
            skSolve(sketch);
        }
        {
            var Q0;
            Q0 = qSketchRegion(id + "F16", true);
            extrude(context, id + "F17", {"entities" : qUnion([Q0]), "operationType" : NewBodyOperationType.REMOVE, "oppositeDirection" : true, "depth" : 25.4 * mm});
        }
    });
